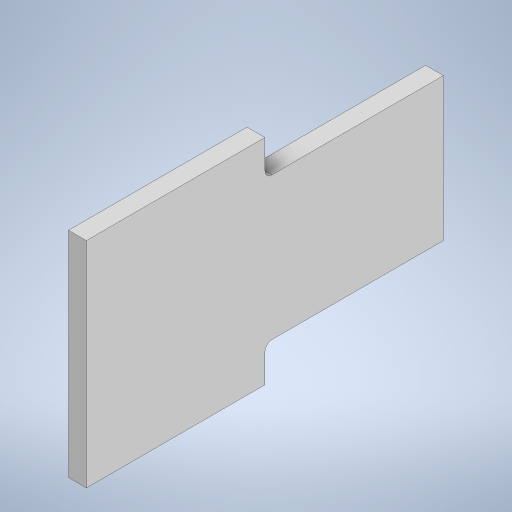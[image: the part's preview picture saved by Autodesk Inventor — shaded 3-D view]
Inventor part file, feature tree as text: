
AUTODESK INVENTOR PART (.ipt)
format: ipt  version: 2023 (Build 270158000, 158)  size: 287,744 bytes
history: native  units: mm
features: extrude x2, sketch x1, fillet x1
ambient origin geometry x8: Origin, YZ Plane, XZ Plane, XY Plane, X Axis, Y Axis, Z Axis, Center Point
bodies: Solido1 (feature_tree)
feature tree (4):
  sketch  "Schizzo1"
  extrude  "Estrusione1"  Depth=120.0mm
  extrude  "Estrusione2"  Depth=10.0mm
  fillet  "Raccordo1"  Radius=80.0mm
